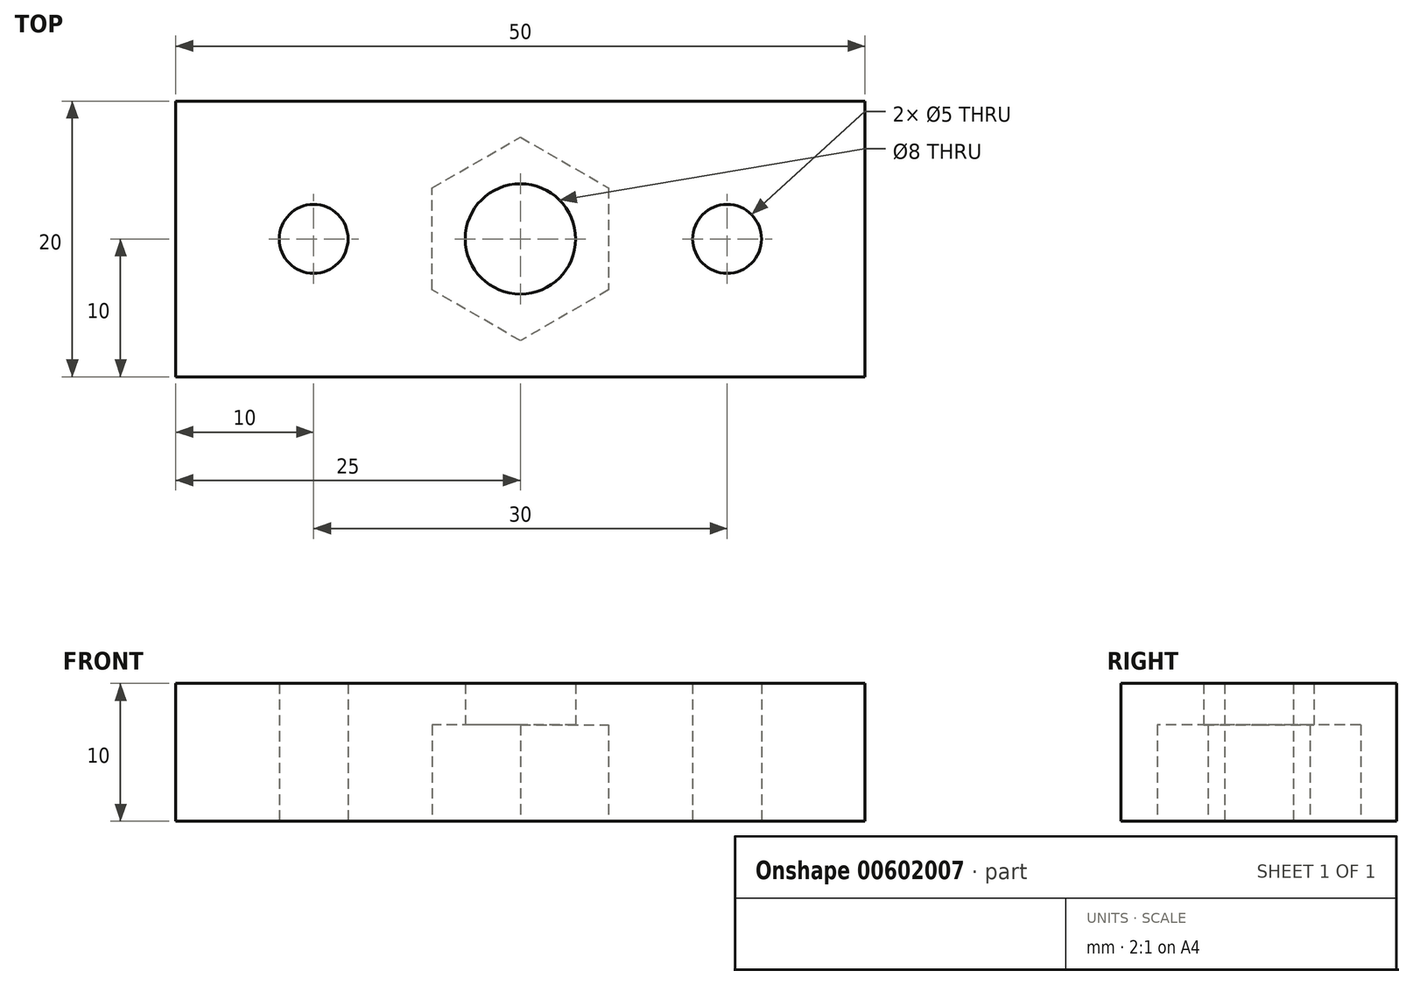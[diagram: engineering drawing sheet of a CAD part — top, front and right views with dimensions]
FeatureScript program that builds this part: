
annotation { "Feature Type Name" : "Feature", "Feature Type Description" : "" }
export const myFeature = defineFeature(function(context is Context, id is Id, definition is map)
    precondition{}
    {
        {
            var Q0;
            Q0=qCreatedBy(makeId("Top.planeOp"),FACE);
            var sketch = newSketch(context, id + "F0", { "sketchPlane" : qUnion([Q0])});
            skCircle(sketch, "E0.cCircle", {"center": v(0, 0) * mm, "radius": 6.4 * mm, "construction": true});
            skLineSegment(sketch, "E0.0", {"start": v(6.4, 3.7) * mm, "end": v(6.4, -3.7) * mm});
            skLineSegment(sketch, "E0.1", {"start": v(6.4, -3.7) * mm, "end": v(0, -7.4) * mm});
            skLineSegment(sketch, "E0.2", {"start": v(0, -7.4) * mm, "end": v(-6.4, -3.7) * mm});
            skLineSegment(sketch, "E0.3", {"start": v(-6.4, -3.7) * mm, "end": v(-6.4, 3.7) * mm});
            skLineSegment(sketch, "E0.4", {"start": v(-6.4, 3.7) * mm, "end": v(0, 7.4) * mm});
            skLineSegment(sketch, "E0.5", {"start": v(0, 7.4) * mm, "end": v(6.4, 3.7) * mm});
            skPoint(sketch, "E0.0.midPoint", {"position": v(6.4, 0) * mm});
            skLineSegment(sketch, "E1.bottom", {"start": v(25, 10) * mm, "end": v(-25, 10) * mm});
            skLineSegment(sketch, "E1.top", {"start": v(25, -10) * mm, "end": v(-25, -10) * mm});
            skLineSegment(sketch, "E1.left", {"start": v(25, 10) * mm, "end": v(25, -10) * mm});
            skLineSegment(sketch, "E1.right", {"start": v(-25, 10) * mm, "end": v(-25, -10) * mm});
            skLineSegment(sketch, "E2.bottom", {"start": v(25, 10) * mm, "end": v(15, 10) * mm});
            skLineSegment(sketch, "E2.top", {"start": v(25, 0) * mm, "end": v(15, 0) * mm});
            skLineSegment(sketch, "E2.left", {"start": v(25, 10) * mm, "end": v(25, 0) * mm});
            skLineSegment(sketch, "E2.right", {"start": v(15, 10) * mm, "end": v(15, 0) * mm});
            skLineSegment(sketch, "E3.bottom", {"start": v(-25, 10) * mm, "end": v(-15, 10) * mm});
            skLineSegment(sketch, "E3.top", {"start": v(-25, 0) * mm, "end": v(-15, 0) * mm});
            skLineSegment(sketch, "E3.left", {"start": v(-25, 10) * mm, "end": v(-25, 0) * mm});
            skLineSegment(sketch, "E3.right", {"start": v(-15, 10) * mm, "end": v(-15, 0) * mm});
            skCircle(sketch, "E4", {"center": v(-15, 0) * mm, "radius": 2.5 * mm});
            skCircle(sketch, "E5", {"center": v(15, 0) * mm, "radius": 2.5 * mm});
            skSolve(sketch);
        }
        {
            var Q0;
            Q0 = qSketchRegion(id + "F0", true);
            extrude(context, id + "F1", {"entities" : qUnion([Q0]), "depth" : 7 * mm, "offsetDistance" : 25.4 * mm});
        }
        {
            var Q0;
            Q0=makeQuery(id+"F1.opExtrude","CAP_FACE",FACE,{"disambiguationData":[OSD([sQuery(id+"F0.wireOp",EDGE,"E0.0"),sQuery(id+"F0.wireOp",EDGE,"E0.1"),sQuery(id+"F0.wireOp",EDGE,"E0.2"),sQuery(id+"F0.wireOp",EDGE,"E0.3"),sQuery(id+"F0.wireOp",EDGE,"E0.4"),sQuery(id+"F0.wireOp",EDGE,"E0.5"),sQuery(id+"F0.wireOp",EDGE,"E1.bottom"),sQuery(id+"F0.wireOp",EDGE,"E1.top"),sQuery(id+"F0.wireOp",EDGE,"E1.left"),sQuery(id+"F0.wireOp",EDGE,"E1.right"),sQuery(id+"F0.wireOp",EDGE,"E2.bottom"),sQuery(id+"F0.wireOp",EDGE,"E2.left"),sQuery(id+"F0.wireOp",EDGE,"E3.bottom"),sQuery(id+"F0.wireOp",EDGE,"E3.left"),sQuery(id+"F0.wireOp",EDGE,"E4"),sQuery(id+"F0.wireOp",EDGE,"E5")])],"isStart":false});
            var sketch = newSketch(context, id + "F2", { "sketchPlane" : qUnion([Q0])});
            skLineSegment(sketch, "E6.bottom", {"start": v(-25, 10) * mm, "end": v(25, 10) * mm});
            skLineSegment(sketch, "E6.top", {"start": v(-25, -10) * mm, "end": v(25, -10) * mm});
            skLineSegment(sketch, "E6.left", {"start": v(-25, 10) * mm, "end": v(-25, -10) * mm});
            skLineSegment(sketch, "E6.right", {"start": v(25, 10) * mm, "end": v(25, -10) * mm});
            skCircle(sketch, "E7", {"center": v(0, 0) * mm, "radius": 4 * mm});
            skSolve(sketch);
        }
        {
            var Q0;
            Q0=makeQuery(id+"F2.imprint","IMPRINT",FACE,{"disambiguationData":[TD([[makeQuery(id+"F2.imprint","IMPRINT",EDGE,{"derivedFrom":sQuery(id+"F2.wireOp",EDGE,"E7")}),-1.0]])]});
            var Q1;
            Q1=makeQuery(id+"F2.imprint","IMPRINT",FACE,{"disambiguationData":[TD([[makeQuery(id+"F2.imprint","IMPRINT",EDGE,{"derivedFrom":sQuery(id+"F2.wireOp",EDGE,"E6.bottom")}),1.0]])]});
            extrude(context, id + "F3", {"entities" : qUnion([Q0, Q1]), "operationType" : NewBodyOperationType.ADD, "depth" : 3 * mm, "offsetDistance" : 25.4 * mm});
        }
    });
